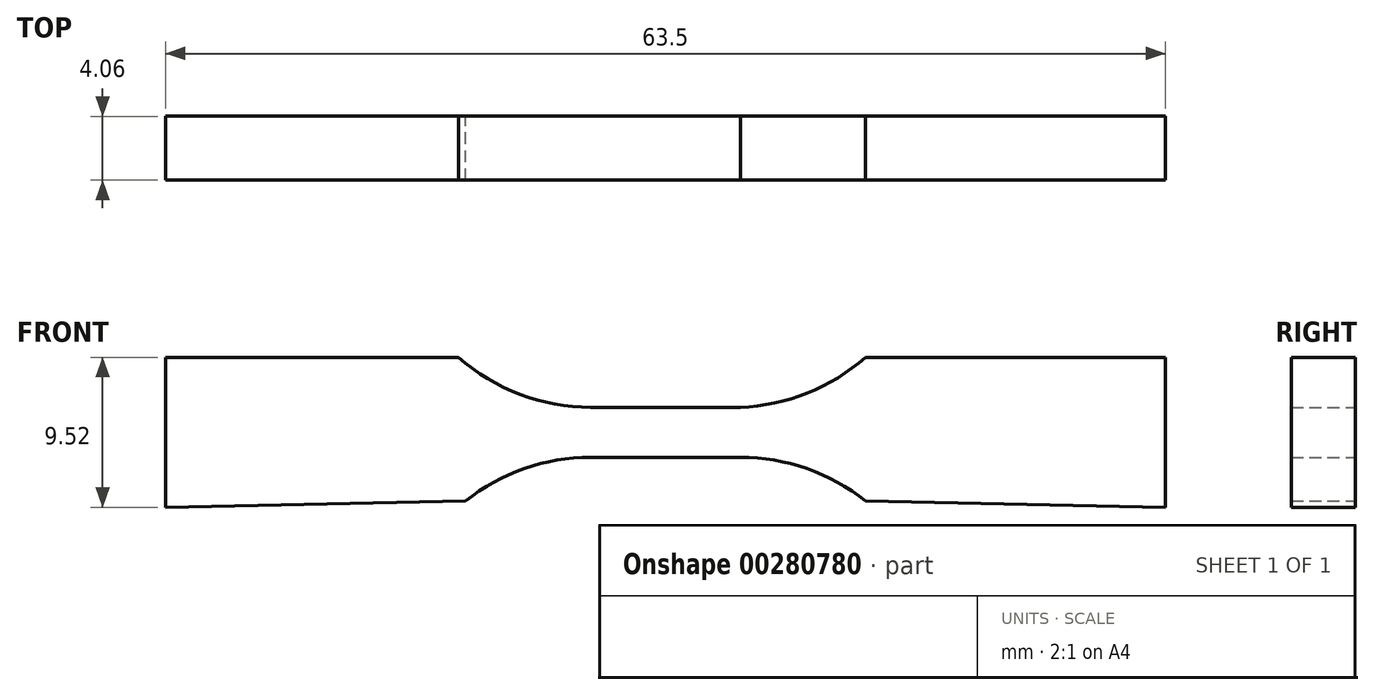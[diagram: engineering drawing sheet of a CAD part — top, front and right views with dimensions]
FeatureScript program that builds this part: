
annotation { "Feature Type Name" : "Feature", "Feature Type Description" : "" }
export const myFeature = defineFeature(function(context is Context, id is Id, definition is map)
    precondition{}
    {
        {
            var Q0;
            Q0=qCreatedBy(makeId("Front.planeOp"),FACE);
            var sketch = newSketch(context, id + "F0", { "sketchPlane" : qUnion([Q0])});
            skLineSegment(sketch, "E0", {"start": v(0, 1.59) * mm, "end": v(4.76, 1.59) * mm});
            skLineSegment(sketch, "E1", {"start": v(12.7, 4.76) * mm, "end": v(31.75, 4.76) * mm});
            skLineSegment(sketch, "E2.MirrorCS", {"start": v(12.7, -4.37) * mm, "end": v(31.75, -4.76) * mm});
            skLineSegment(sketch, "E3.MirrorCS", {"start": v(0, -1.59) * mm, "end": v(4.76, -1.59) * mm});
            skLineSegment(sketch, "E4.MirrorCS", {"start": v(0, -1.59) * mm, "end": v(-4.76, -1.59) * mm});
            skLineSegment(sketch, "E5.MirrorCS", {"start": v(-12.7, 4.76) * mm, "end": v(-31.75, 4.76) * mm});
            skLineSegment(sketch, "E6.MirrorCS", {"start": v(-12.7, -4.37) * mm, "end": v(-31.75, -4.76) * mm});
            skLineSegment(sketch, "E7.MirrorCS", {"start": v(0, 1.59) * mm, "end": v(-4.76, 1.59) * mm});
            skLineSegment(sketch, "E8", {"start": v(-31.75, 4.76) * mm, "end": v(-31.75, -4.76) * mm});
            skLineSegment(sketch, "E9", {"start": v(31.75, 4.76) * mm, "end": v(31.75, -4.76) * mm});
            skArc(sketch, "E10", {"start": v(-13.52, 5.1) * mm, "mid": v(-9.48, 2.5) * mm, "end": v(-4.76, 1.59) * mm});
            skArc(sketch, "E11", {"start": v(-4.76, -1.59) * mm, "mid": v(-8.97, -2.3) * mm, "end": v(-12.7, -4.37) * mm});
            skArc(sketch, "E12", {"start": v(4.76, 1.59) * mm, "mid": v(9, 2.49) * mm, "end": v(12.7, 4.76) * mm});
            skArc(sketch, "E13", {"start": v(12.7, -4.37) * mm, "mid": v(8.97, -2.3) * mm, "end": v(4.76, -1.59) * mm});
            skSolve(sketch);
        }
        {
            var Q0;
            Q0 = qSketchRegion(id + "F0", true);
            extrude(context, id + "F1", {"entities" : qUnion([Q0]), "endBound" : BoundingType.SYMMETRIC, "depth" : 4.06 * mm});
        }
    });
